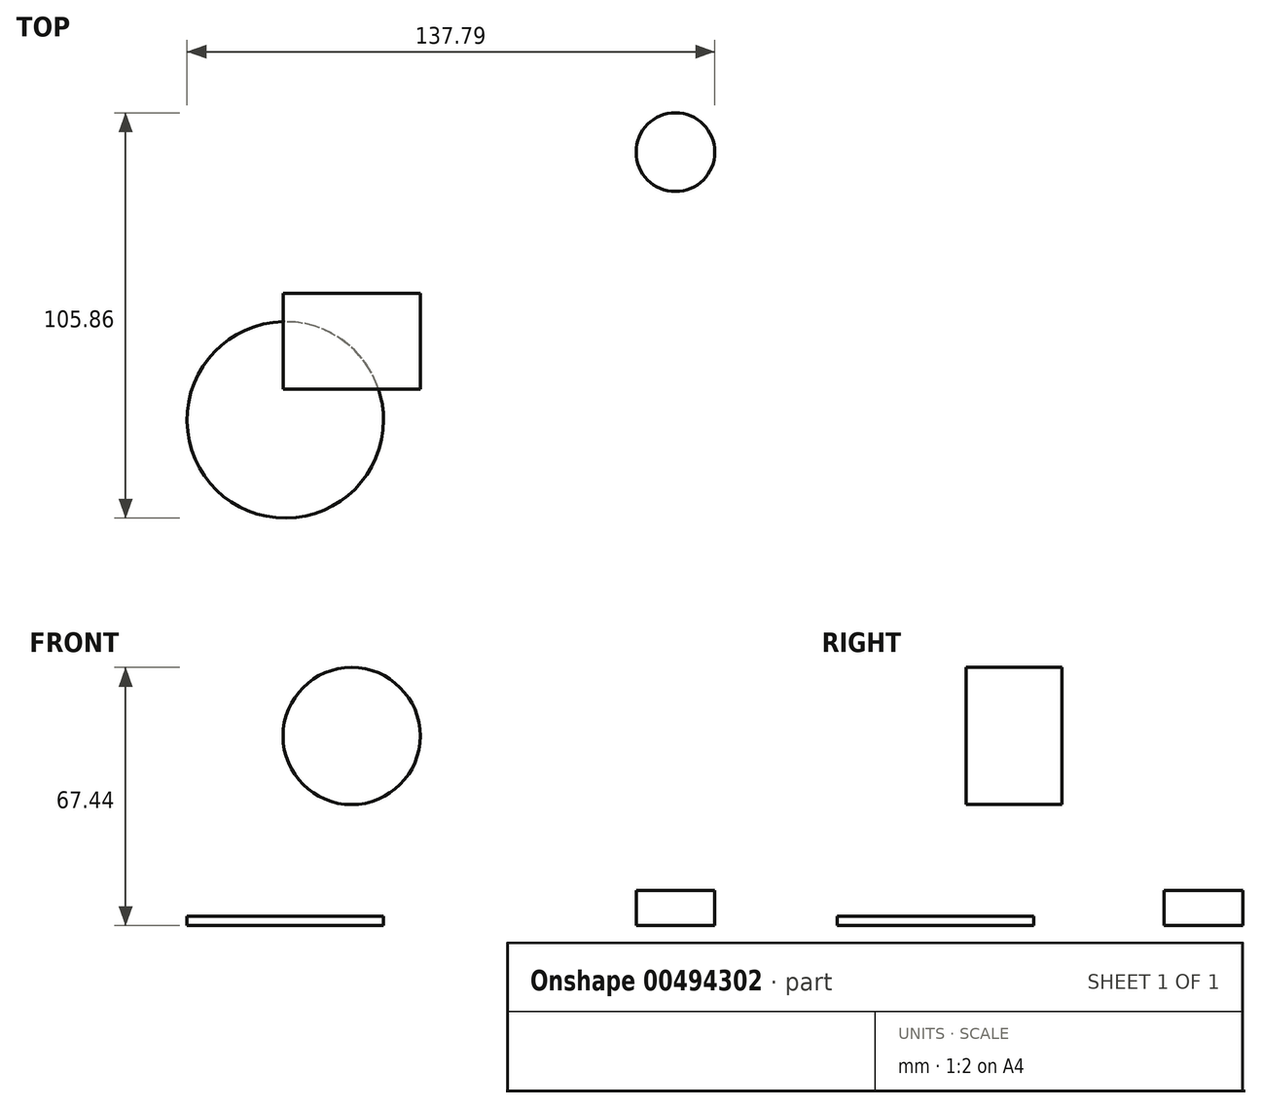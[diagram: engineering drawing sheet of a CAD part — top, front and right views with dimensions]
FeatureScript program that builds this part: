
annotation { "Feature Type Name" : "Feature", "Feature Type Description" : "" }
export const myFeature = defineFeature(function(context is Context, id is Id, definition is map)
    precondition{}
    {
        {
            var Q0;
            Q0=qCreatedBy(makeId("Top.planeOp"),FACE);
            var sketch = newSketch(context, id + "F0", { "sketchPlane" : qUnion([Q0])});
            skCircle(sketch, "E0", {"center": v(37.47, 36.94) * mm, "radius": 10.27 * mm});
            skSolve(sketch);
        }
        {
            var Q0;
            Q0 = qSketchRegion(id + "F0", true);
            extrude(context, id + "F1", {"entities" : qUnion([Q0]), "depth" : 9.16 * mm, "offsetDistance" : 25 * mm});
        }
        {
            var Q0;
            Q0=qCreatedBy(makeId("Top.planeOp"),FACE);
            var sketch = newSketch(context, id + "F2", { "sketchPlane" : qUnion([Q0])});
            skCircle(sketch, "E1", {"center": v(-64.4, -33) * mm, "radius": 25.65 * mm});
            skSolve(sketch);
        }
        {
            var Q0;
            Q0 = qSketchRegion(id + "F2", true);
            extrude(context, id + "F3", {"entities" : qUnion([Q0]), "depth" : 2.5 * mm, "offsetDistance" : 25 * mm});
        }
        {
            var Q0;
            Q0=qCreatedBy(makeId("Front.planeOp"),FACE);
            var sketch = newSketch(context, id + "F4", { "sketchPlane" : qUnion([Q0])});
            skCircle(sketch, "E2", {"center": v(-47.08, 49.52) * mm, "radius": 17.91 * mm});
            skSolve(sketch);
        }
        {
            var Q0;
            Q0 = qSketchRegion(id + "F4", true);
            extrude(context, id + "F5", {"entities" : qUnion([Q0]), "depth" : 25 * mm, "offsetDistance" : 25 * mm});
        }
        {
            var Q0;
            Q0=qCreatedBy(makeId("Top.planeOp"),FACE);
            var sketch = newSketch(context, id + "F6", { "sketchPlane" : qUnion([Q0])});
            skCircle(sketch, "E3", {"center": v(-37.1, 33.62) * mm, "radius": 19.52 * mm});
            skSolve(sketch);
        }
        {
            var Q0;
            Q0=sQuery(id+"F6.wireOp",EDGE,"E3");
            extrude(context, id + "F7", {"bodyType" : ToolBodyType.SURFACE, "surfaceEntities" : qUnion([Q0]), "depth" : 10 * mm, "offsetDistance" : 25 * mm});
        }
    });
